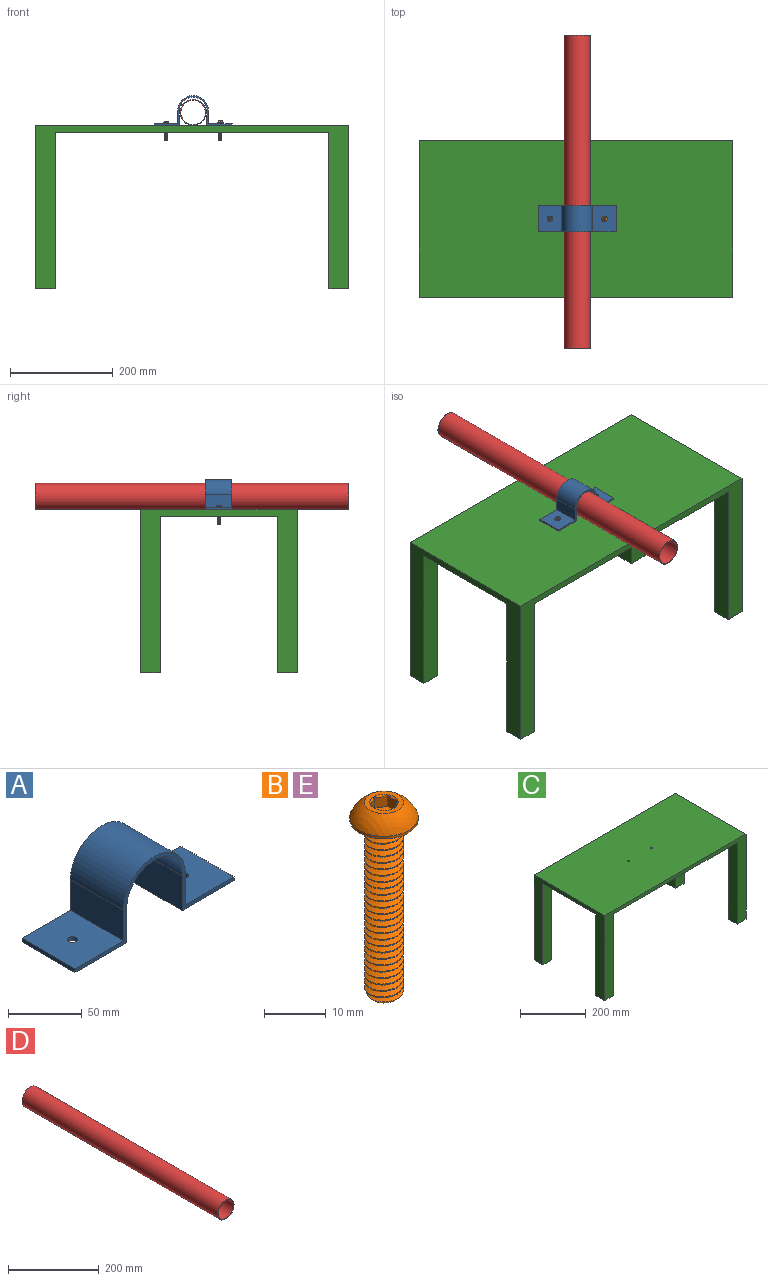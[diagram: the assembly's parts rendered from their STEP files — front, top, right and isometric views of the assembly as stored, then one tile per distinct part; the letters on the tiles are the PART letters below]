
ASSEMBLY  parts=5 mates=4
PART A: 16 faces, bbox 152.4x50.8x58.4 mm
  f0: plane 50.8x49.53mm, normal (0,0,-1), area 2480.3mm2, adj f5,f10,f12,f13,f14
  f1: plane 50.8x25.4mm, normal (-1,0,0), area 1290.3mm2, adj f2,f11,f12,f13
  f2: plane 50.8x46.36mm, normal (0,0,1), area 2319mm2, adj f1,f3,f12,f13,f15
  f3: plane 50.8x3.18mm, normal (-1,0,0), area 161.3mm2, adj f2,f4,f12,f13
  f4: plane 50.8x49.53mm, normal (0,0,-1), area 2480.3mm2, adj f3,f8,f12,f13,f15
  f5: plane 50.8x3.18mm, normal (1,0,0), area 161.3mm2, adj f0,f6,f12,f13
  f6: plane 50.8x46.36mm, normal (0,0,1), area 2319mm2, adj f5,f7,f12,f13,f14
  f7: plane 50.8x25.4mm, normal (1,0,0), area 1290.3mm2, adj f6,f11,f12,f13
  f8: plane 50.8x28.58mm, normal (1,0,0), area 1451.6mm2, adj f4,f9,f12,f13
  f9: cylinder r=26.67mm len=53.34mm, axis (0,1,0), area 4256.3mm2, adj f8,f10,f12,f13
  f10: plane 50.8x28.58mm, normal (-1,0,0), area 1451.6mm2, adj f0,f9,f12,f13
  f11: cylinder r=29.84mm len=59.69mm, axis (0,1,0), area 4763.1mm2, adj f1,f7,f12,f13
  f12: plane 152.4x58.42mm, normal (0,-1,0), area 757.7mm2, adj f0,f1,f2,f3,f4,f5,f6,f7
  f13: plane 152.4x58.42mm, normal (0,1,0), area 757.7mm2, adj f0,f1,f2,f3,f4,f5,f6,f7
  f14: cylinder r=3.38mm len=6.76mm, axis (0,0,1), area 67.4mm2, adj f0,f6
  f15: cylinder r=3.38mm len=6.76mm, axis (0,0,1), area 67.4mm2, adj f2,f4
PART B: 23 faces, bbox 12x12x40.5 mm
  f0: cone r=2.29mm half-angle=45deg, axis (0,0,1), area 0.5mm2, adj f9,f17
  f1: cylinder r=5.55mm len=11.1mm, axis (0,0,1), area 17.5mm2, adj f2,f10
  f2: sphere r=5.97mm, area 107mm2, adj f1,f9
  f3: cone r=2.22mm half-angle=45deg, axis (0,0,1), area 12.3mm2, adj f4,f5,f6,f7,f8
  f4: cylinder r=3.17mm len=33.97mm, axis (0,0,-1), area 84.7mm2, adj f3,f6,f8,f10
  f5: plane 4.45x4.45mm, normal (0,0,-1), area 15.5mm2, adj f3
  f6: bspline ~35.27x6.35mm, area 447.6mm2, adj f3,f4,f7,f10
  f7: cylinder r=2.35mm len=34.8mm, axis (0,0,-1), area 64.1mm2, adj f3,f6,f8,f10
  f8: bspline ~35.88x6.35mm, area 448.2mm2, adj f3,f4,f7,f10
  f9: plane 7.1x7.1mm, normal (0,0,1), area 15.2mm2, adj f0,f2,f11,f12,f13,f14,f15
  f10: plane 11.58x11.58mm, normal (0,0,-1), area 72.5mm2, adj f1,f4,f6,f7,f8
  f11: cone r=2.29mm half-angle=45deg, axis (0,0,1), area 0mm2, adj f9,f18
  f12: cone r=2.29mm half-angle=45deg, axis (0,0,1), area 0mm2, adj f9,f19
  f13: cone r=2.29mm half-angle=45deg, axis (0,0,1), area 0mm2, adj f9,f20
  f14: cone r=2.29mm half-angle=45deg, axis (0,0,1), area 0mm2, adj f9,f21
  f15: cone r=2.29mm half-angle=45deg, axis (0,0,1), area 0mm2, adj f9,f22
  f16: plane 4.58x3.97mm, normal (0,0,1), area 13.6mm2, adj f17,f18,f19,f20,f21,f22
  f17: plane 2.57x2.51mm, normal (-1,0,0), area 4.9mm2, adj f0,f16,f18,f22
  f18: plane 3.22x2.85mm, normal (-0.5,-0.87,0), area 4.9mm2, adj f11,f16,f17,f19
  f19: plane 3.22x2.85mm, normal (0.5,-0.87,0), area 4.9mm2, adj f12,f16,f18,f20
  f20: plane 3.22x3.16mm, normal (1,0,0), area 4.9mm2, adj f13,f16,f19,f21
  f21: plane 3.22x2.85mm, normal (0.5,0.87,0), area 4.9mm2, adj f14,f16,f20,f22
  f22: plane 3.22x2.85mm, normal (-0.5,0.87,0), area 4.9mm2, adj f15,f16,f17,f21
PART C: 20 faces, bbox 609.6x304.8x317.5 mm
  f0: plane 609.6x317.5mm, normal (0,1,0), area 30967.7mm2, adj f1,f3,f4,f5,f13,f14,f15,f17
  f1: plane 317.5x304.8mm, normal (-1,0,0), area 27096.7mm2, adj f0,f2,f4,f5,f6,f8,f12,f14
  f2: plane 609.6x317.5mm, normal (0,-1,0), area 30967.7mm2, adj f1,f3,f4,f5,f7,f8,f9,f11
  f3: plane 317.5x304.8mm, normal (1,0,0), area 27096.7mm2, adj f0,f2,f4,f5,f10,f11,f16,f17
  f4: plane 609.6x304.8mm, normal (0,0,1), area 185734.4mm2, adj f0,f1,f2,f3,f18,f19
  f5: plane 609.6x304.8mm, normal (0,0,-1), area 179927.9mm2, adj f0,f1,f2,f3,f6,f7,f9,f10
  f6: plane 304.8x38.1mm, normal (0,1,0), area 11612.9mm2, adj f1,f5,f7,f8
  f7: plane 304.8x38.1mm, normal (1,0,0), area 11612.9mm2, adj f2,f5,f6,f8
  f8: plane 38.1x38.1mm, normal (0,0,-1), area 1451.6mm2, adj f1,f2,f6,f7
  f9: plane 304.8x38.1mm, normal (-1,0,0), area 11612.9mm2, adj f2,f5,f10,f11
  f10: plane 304.8x38.1mm, normal (0,1,0), area 11612.9mm2, adj f3,f5,f9,f11
  f11: plane 38.1x38.1mm, normal (0,0,-1), area 1451.6mm2, adj f2,f3,f9,f10
  f12: plane 304.8x38.1mm, normal (0,-1,0), area 11612.9mm2, adj f1,f5,f13,f14
  f13: plane 304.8x38.1mm, normal (1,0,0), area 11612.9mm2, adj f0,f5,f12,f14
  f14: plane 38.1x38.1mm, normal (0,0,-1), area 1451.6mm2, adj f0,f1,f12,f13
  f15: plane 304.8x38.1mm, normal (-1,0,0), area 11612.9mm2, adj f0,f5,f16,f17
  f16: plane 304.8x38.1mm, normal (0,-1,0), area 11612.9mm2, adj f3,f5,f15,f17
  f17: plane 38.1x38.1mm, normal (0,0,-1), area 1451.6mm2, adj f0,f3,f15,f16
  f18: cylinder r=3.38mm len=12.7mm, axis (0,0,1), area 269.6mm2, adj f4,f5
  f19: cylinder r=3.38mm len=12.7mm, axis (0,0,1), area 269.6mm2, adj f4,f5
PART D: 4 faces, bbox 50.8x609.6x50.8 mm
  f0: cylinder r=23.81mm len=609.6mm, axis (0,1,0), area 91207.3mm2, adj f2,f3
  f1: cylinder r=25.4mm len=609.6mm, axis (0,1,0), area 97287.8mm2, adj f2,f3
  f2: plane 50.8x50.8mm, normal (0,-1,0), area 245.4mm2, adj f0,f1
  f3: plane 50.8x50.8mm, normal (0,1,0), area 245.4mm2, adj f0,f1
PART E: same geometry as B
PLACE A t=(3.43,3.93,99.75)mm
PLACE B t=(56.45,3.93,107.36)mm
PLACE C t=(1.21,3.93,85.46)mm fixed
PLACE D t=(3.43,56.27,123.56)mm
PLACE E t=(-49.59,3.93,106.86)mm
MATE fastened C.f19 <-> A.f15  axis (0,0,1) through (-49.59,3.93,98.16)mm
MATE fastened A.f14 <-> B.f0  axis (0,0,1) through (56.45,3.93,101.34)mm
MATE fastened A.f15 <-> E.f0  axis (0,0,1) through (-49.59,3.93,101.34)mm
MATE slider D.f1 <-> A.f12  axis (0,-1,0) through (3.43,-248.53,123.56)mm
